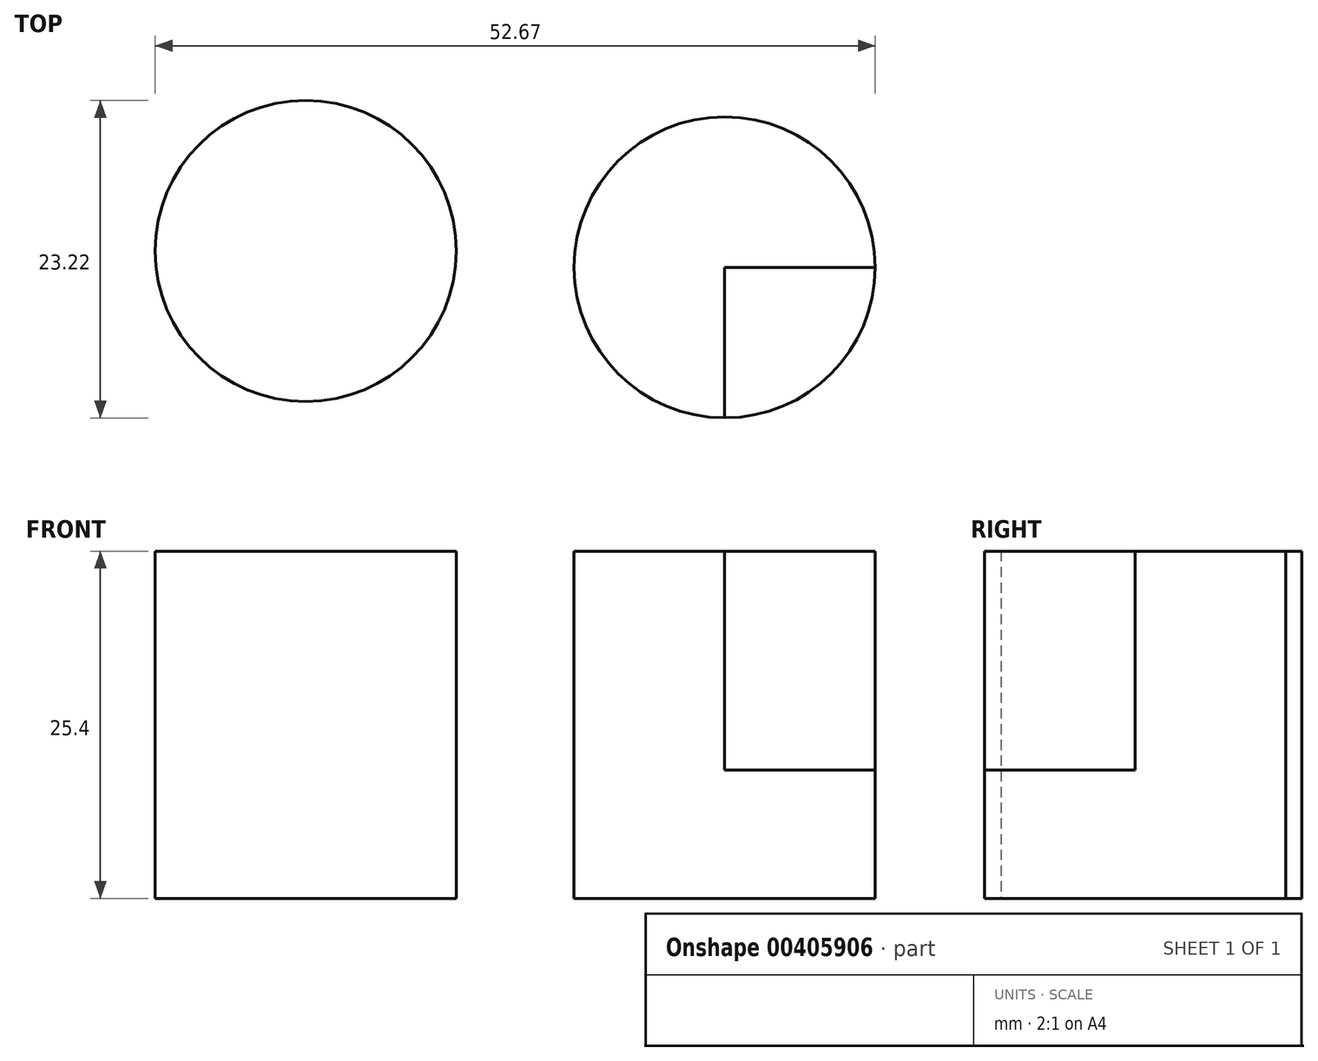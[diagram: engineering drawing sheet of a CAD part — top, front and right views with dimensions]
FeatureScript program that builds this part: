
annotation { "Feature Type Name" : "Feature", "Feature Type Description" : "" }
export const myFeature = defineFeature(function(context is Context, id is Id, definition is map)
    precondition{}
    {
        {
            var Q0;
            Q0=qCreatedBy(makeId("Top.planeOp"),FACE);
            var sketch = newSketch(context, id + "F0", { "sketchPlane" : qUnion([Q0])});
            skCircle(sketch, "E0", {"center": v(-59.87, -46.61) * mm, "radius": 11.01 * mm});
            skCircle(sketch, "E1", {"center": v(-29.22, -47.8) * mm, "radius": 11.01 * mm});
            skLineSegment(sketch, "E2", {"start": v(0, 0) * mm, "end": v(0, 50.8) * mm});
            skSolve(sketch);
        }
        {
            var Q0;
            Q0 = qSketchRegion(id + "F0", true);
            extrude(context, id + "F1", {"entities" : qUnion([Q0]), "depth" : 25.4 * mm});
        }
        {
            var Q0;
            Q0=makeQuery(id+"F1.opExtrude","CAP_FACE",FACE,{"disambiguationData":[OSD([sQuery(id+"F0.wireOp",EDGE,"E1")])],"isStart":false});
            var sketch = newSketch(context, id + "F2", { "sketchPlane" : qUnion([Q0])});
            skLineSegment(sketch, "E3.bottom", {"start": v(-29.22, -47.8) * mm, "end": v(-6.54, -47.8) * mm});
            skLineSegment(sketch, "E3.top", {"start": v(-29.22, -61.33) * mm, "end": v(-6.54, -61.33) * mm});
            skLineSegment(sketch, "E3.left", {"start": v(-29.22, -47.8) * mm, "end": v(-29.22, -61.33) * mm});
            skLineSegment(sketch, "E3.right", {"start": v(-6.54, -47.8) * mm, "end": v(-6.54, -61.33) * mm});
            skSolve(sketch);
        }
        {
            var Q0;
            {var subQ0=sQuery(id+"F2.wireOp",EDGE,"E3.left");var subQ1=sQuery(id+"F2.wireOp",EDGE,"E3.bottom");var subQ2=makeQuery(id+"F2.imprint","INTERSECT",VERTEX,{"derivedFrom":[subQ1,subQ0]});Q0=makeQuery(id+"F2.imprint","IMPRINT",FACE,{"disambiguationData":[TD([[makeQuery(id+"F2.imprint","IMPRINT",EDGE,{"disambiguationData":[TD([[subQ2,-1.0]])],"derivedFrom":subQ1}),-1.0]])]});}
            extrude(context, id + "F3", {"entities" : qUnion([Q0]), "operationType" : NewBodyOperationType.REMOVE, "oppositeDirection" : true, "depth" : 16 * mm});
        }
    });
